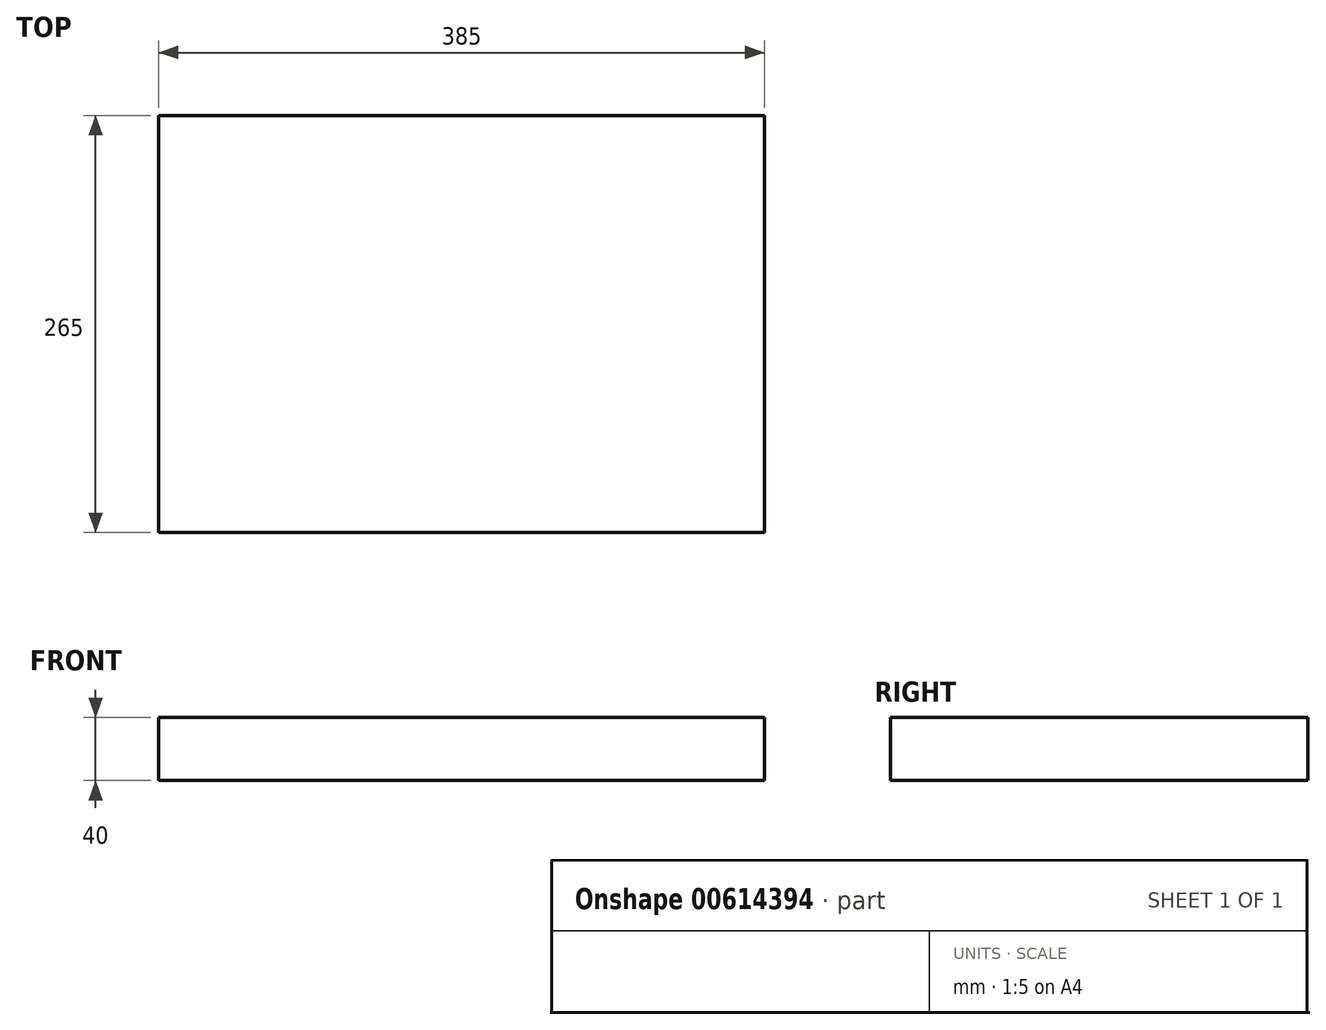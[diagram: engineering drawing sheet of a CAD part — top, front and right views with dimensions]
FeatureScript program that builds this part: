
annotation { "Feature Type Name" : "Feature", "Feature Type Description" : "" }
export const myFeature = defineFeature(function(context is Context, id is Id, definition is map)
    precondition{}
    {
        {
            assignVariable(context, id + "F0", {"name" : "led_h", "anyValue" : 40});
        }
        {
            var Q0;
            Q0=qCreatedBy(makeId("Top.planeOp"),FACE);
            var sketch = newSketch(context, id + "F1", { "sketchPlane" : qUnion([Q0])});
            skLineSegment(sketch, "E0.bottom", {"start": v(-192.04, 76.64) * mm, "end": v(192.96, 76.64) * mm});
            skLineSegment(sketch, "E0.top", {"start": v(-192.04, -188.36) * mm, "end": v(192.96, -188.36) * mm});
            skLineSegment(sketch, "E0.left", {"start": v(-192.04, 76.64) * mm, "end": v(-192.04, -188.36) * mm});
            skLineSegment(sketch, "E0.right", {"start": v(192.96, 76.64) * mm, "end": v(192.96, -188.36) * mm});
            skSolve(sketch);
        }
        {
            var Q0;
            Q0=makeQuery(id+"F1.imprint","IMPRINT",FACE,{"disambiguationData":[TD([[makeQuery(id+"F1.imprint","IMPRINT",EDGE,{"derivedFrom":sQuery(id+"F1.wireOp",EDGE,"E0.bottom")}),-1.0]])]});
            extrude(context, id + "F2", {"entities" : qUnion([Q0]), "depth" : (getVariable(context, 'led_h')) * mm, "offsetDistance" : 25 * mm});
        }
    });
